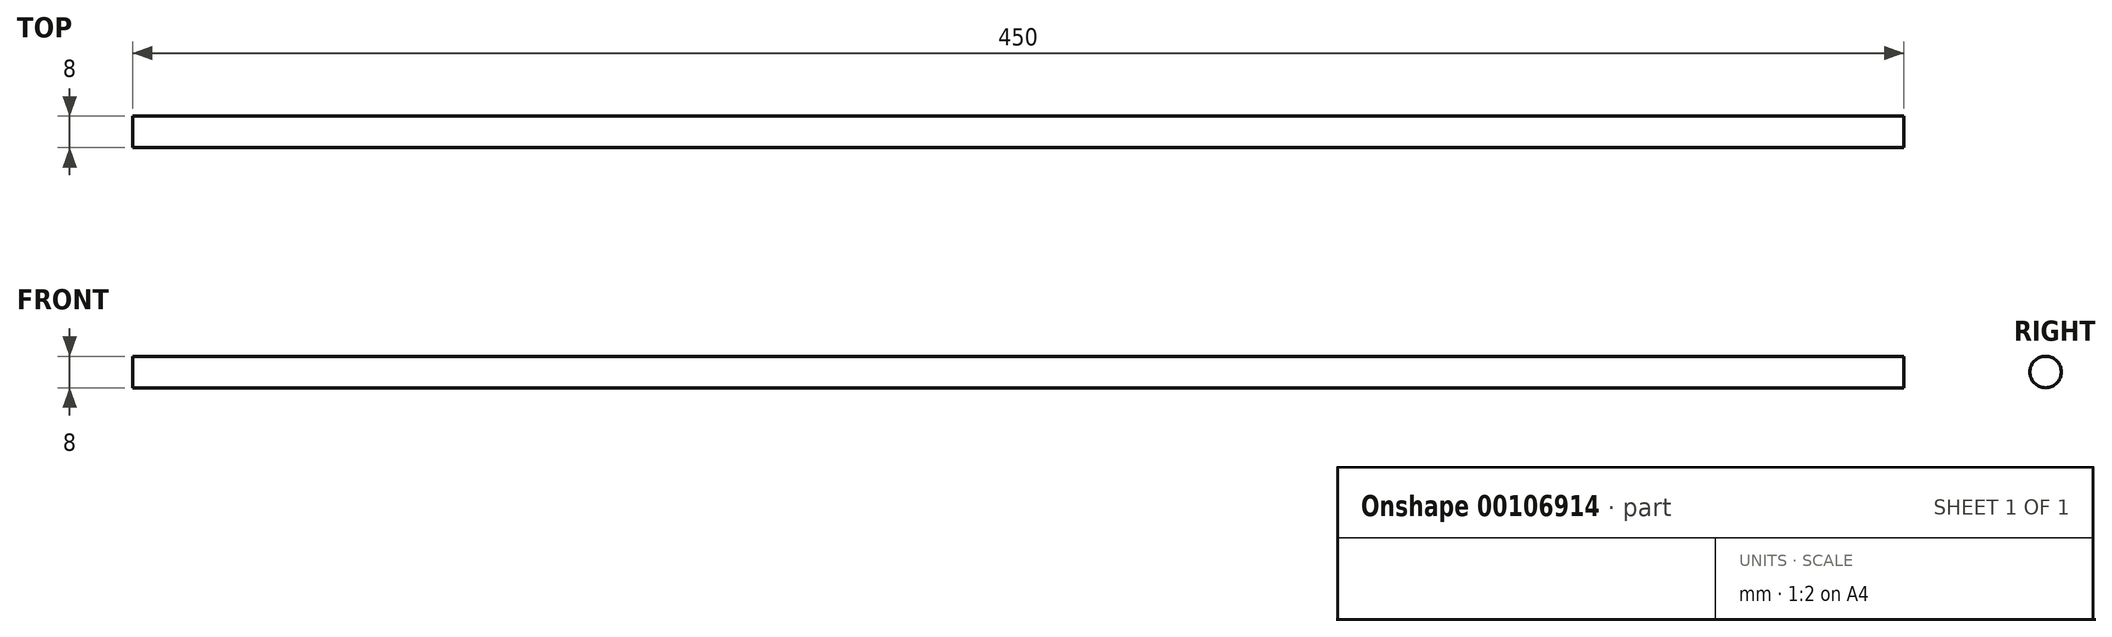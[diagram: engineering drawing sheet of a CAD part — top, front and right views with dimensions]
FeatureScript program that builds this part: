
annotation { "Feature Type Name" : "Feature", "Feature Type Description" : "" }
export const myFeature = defineFeature(function(context is Context, id is Id, definition is map)
    precondition{}
    {
        {
            assignVariable(context, id + "F0", {"name" : "Length", "anyValue" : 450});
        }
        {
            var Q0;
            Q0=qCreatedBy(makeId("Right.planeOp"),FACE);
            var sketch = newSketch(context, id + "F1", { "sketchPlane" : qUnion([Q0])});
            skCircle(sketch, "E0", {"center": v(0, 0) * mm, "radius": 4 * mm});
            skSolve(sketch);
        }
        {
            var Q0;
            Q0 = qSketchRegion(id + "F1", true);
            extrude(context, id + "F2", {"entities" : qUnion([Q0]), "endBound" : BoundingType.SYMMETRIC, "depth" : (getVariable(context, 'Length')) * mm});
        }
    });
